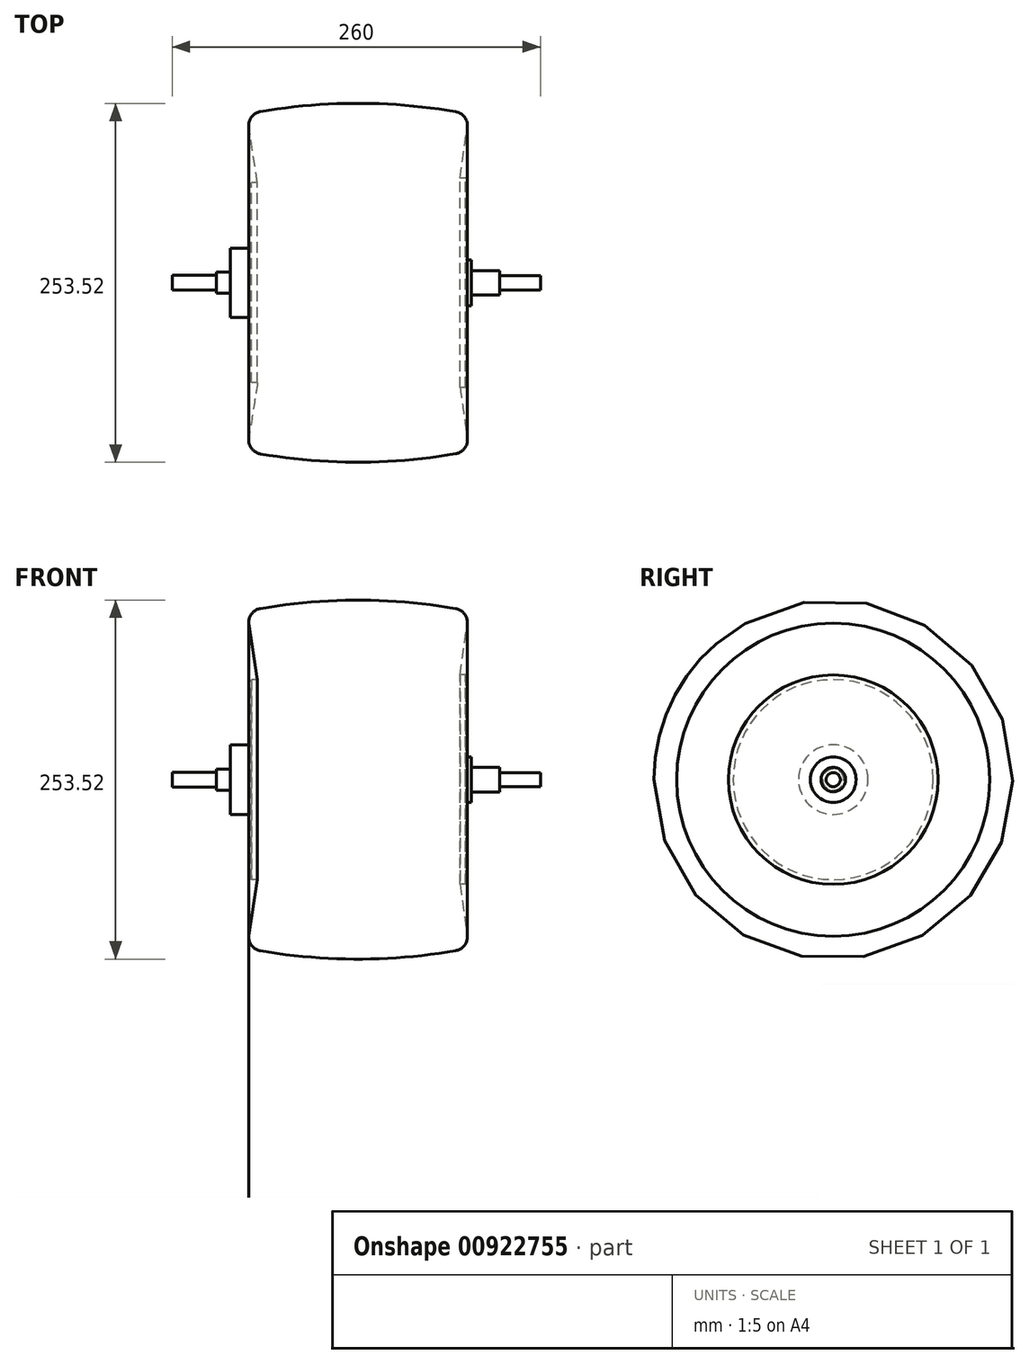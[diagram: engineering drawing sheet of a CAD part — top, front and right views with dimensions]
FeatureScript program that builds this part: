
annotation { "Feature Type Name" : "Feature", "Feature Type Description" : "" }
export const myFeature = defineFeature(function(context is Context, id is Id, definition is map)
    precondition{}
    {
        {
            var Q0;
            Q0=qCreatedBy(makeId("Top.planeOp"),FACE);
            var sketch = newSketch(context, id + "F0", { "sketchPlane" : qUnion([Q0])});
            skLineSegment(sketch, "E0", {"start": v(11.76, 115.13) * mm, "end": v(11.76, 120.4) * mm});
            skLineSegment(sketch, "E1", {"start": v(11.76, 120.4) * mm, "end": v(42.85, 120.4) * mm});
            skLineSegment(sketch, "E2", {"start": v(42.85, 120.4) * mm, "end": v(42.85, 122.57) * mm});
            skLineSegment(sketch, "E3", {"start": v(42.85, 122.57) * mm, "end": v(52.85, 122.57) * mm});
            skLineSegment(sketch, "E4", {"start": v(52.85, 122.57) * mm, "end": v(52.85, 139.67) * mm});
            skLineSegment(sketch, "E5", {"start": v(52.85, 139.67) * mm, "end": v(67.85, 139.67) * mm});
            skLineSegment(sketch, "E6", {"start": v(67.85, 139.67) * mm, "end": v(67.85, 185.77) * mm});
            skLineSegment(sketch, "E7", {"start": v(218.74, 189.11) * mm, "end": v(218.74, 131.26) * mm});
            skLineSegment(sketch, "E8", {"start": v(218.74, 131.26) * mm, "end": v(222.85, 131.26) * mm});
            skLineSegment(sketch, "E9", {"start": v(222.85, 131.26) * mm, "end": v(222.85, 123.77) * mm});
            skLineSegment(sketch, "E10", {"start": v(222.85, 123.77) * mm, "end": v(242.85, 123.77) * mm});
            skLineSegment(sketch, "E11", {"start": v(242.85, 123.77) * mm, "end": v(242.85, 120.13) * mm});
            skLineSegment(sketch, "E12", {"start": v(242.85, 120.13) * mm, "end": v(271.76, 120.13) * mm});
            skLineSegment(sketch, "E13", {"start": v(271.76, 115.13) * mm, "end": v(271.76, 120.13) * mm});
            skArc(sketch, "E14", {"start": v(211.9, 235.95) * mm, "mid": v(142.97, 241.89) * mm, "end": v(74.02, 236.02) * mm});
            skPoint(sketch, "E15.visualSharp", {"position": v(65.26, 234.42) * mm});
            skArc(sketch, "E15.filletArc", {"start": v(74.02, 236.02) * mm, "mid": v(67.9, 232.4) * mm, "end": v(65.73, 225.64) * mm});
            skPoint(sketch, "E16.visualSharp", {"position": v(220.54, 234.36) * mm});
            skArc(sketch, "E16.filletArc", {"start": v(220.2, 225.7) * mm, "mid": v(217.98, 232.38) * mm, "end": v(211.9, 235.95) * mm});
            skLineSegment(sketch, "E17", {"start": v(11.76, 115.13) * mm, "end": v(271.76, 115.13) * mm});
            skLineSegment(sketch, "E18", {"start": v(218.74, 189.11) * mm, "end": v(214.96, 189.11) * mm});
            skLineSegment(sketch, "E19", {"start": v(214.96, 189.11) * mm, "end": v(220.2, 225.7) * mm});
            skLineSegment(sketch, "E20", {"start": v(67.85, 185.77) * mm, "end": v(71.97, 185.77) * mm});
            skLineSegment(sketch, "E21", {"start": v(71.97, 185.77) * mm, "end": v(65.73, 225.64) * mm});
            skSolve(sketch);
        }
        {
            var Q0;
            Q0 = qSketchRegion(id + "F0", true);
            var Q1;
            Q1=sQuery(id+"F0.wireOp",EDGE,"E17");
            revolve(context, id + "F1", {"surfaceOperationType" : NewSurfaceOperationType.NEW, "entities" : qUnion([Q0]), "axis" : qUnion([Q1]), "revolveType" : RevolveType.FULL});
        }
    });
